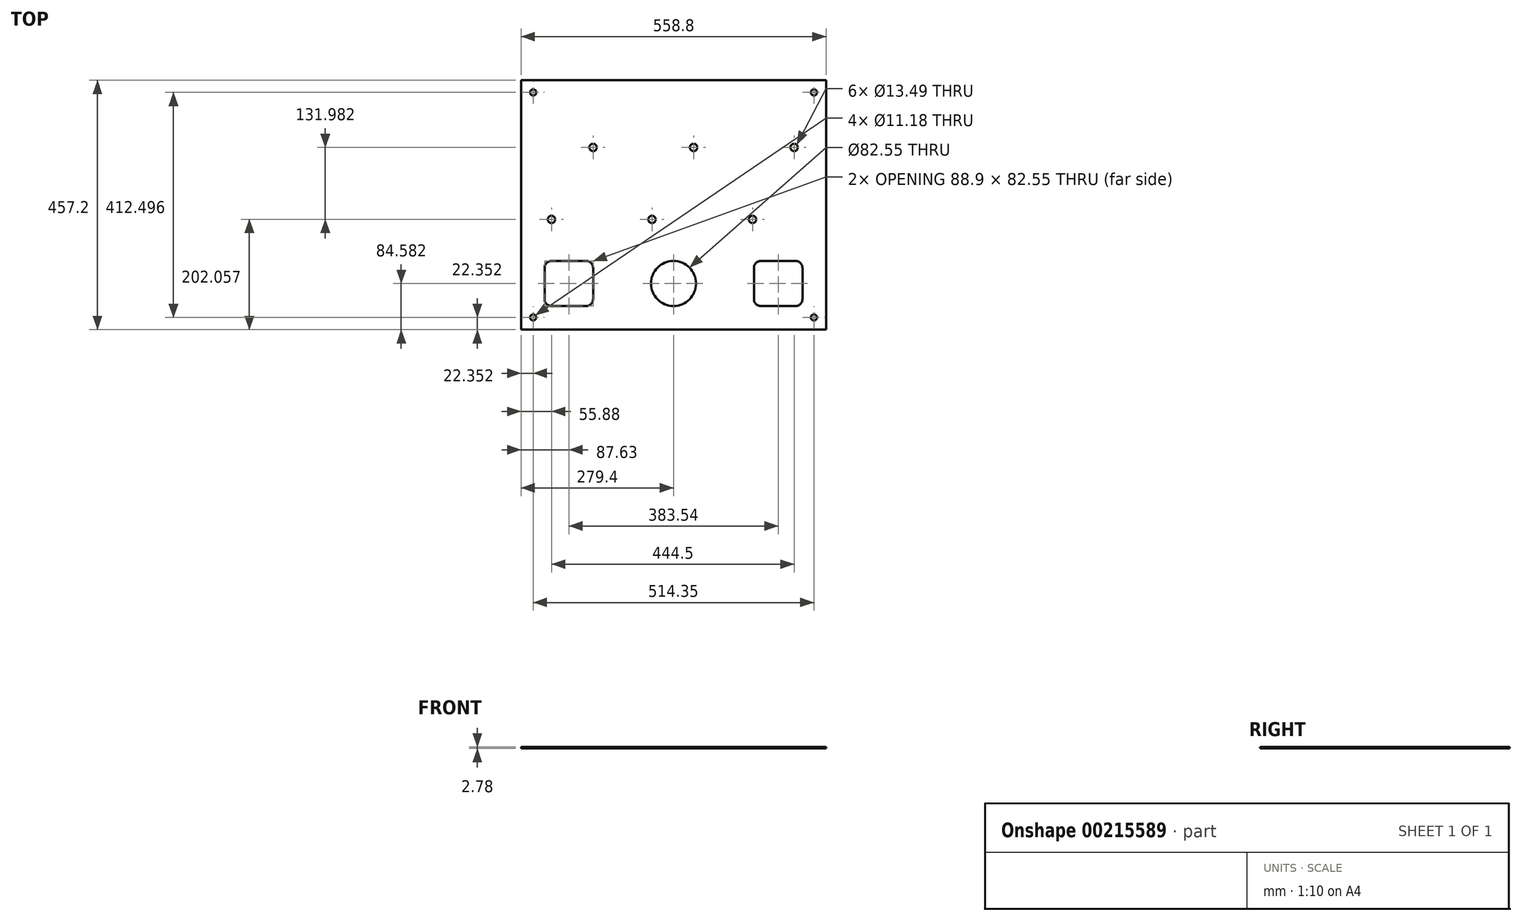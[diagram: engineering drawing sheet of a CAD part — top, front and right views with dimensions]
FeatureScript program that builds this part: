
annotation { "Feature Type Name" : "Feature", "Feature Type Description" : "" }
export const myFeature = defineFeature(function(context is Context, id is Id, definition is map)
    precondition{}
    {
        {
            var Q0;
            Q0=qCreatedBy(makeId("Top.planeOp"),FACE);
            var sketch = newSketch(context, id + "F0", { "sketchPlane" : qUnion([Q0])});
            skLineSegment(sketch, "E0.bottom", {"start": v(0, 0) * mm, "end": v(558.8, 0) * mm});
            skLineSegment(sketch, "E0.top", {"start": v(0, 457.2) * mm, "end": v(558.8, 457.2) * mm});
            skLineSegment(sketch, "E0.left", {"start": v(0, 0) * mm, "end": v(0, 457.2) * mm});
            skLineSegment(sketch, "E0.right", {"start": v(558.8, 0) * mm, "end": v(558.8, 457.2) * mm});
            skCircle(sketch, "E1", {"center": v(22.35, 434.85) * mm, "radius": 5.59 * mm});
            skCircle(sketch, "E2", {"center": v(22.35, 22.35) * mm, "radius": 5.59 * mm});
            skCircle(sketch, "E3", {"center": v(536.7, 22.35) * mm, "radius": 5.59 * mm});
            skCircle(sketch, "E4", {"center": v(536.7, 434.85) * mm, "radius": 5.59 * mm});
            skLineSegment(sketch, "E5.bottom", {"start": v(55.88, 125.86) * mm, "end": v(119.38, 125.86) * mm});
            skLineSegment(sketch, "E5.top", {"start": v(55.88, 43.3) * mm, "end": v(119.38, 43.3) * mm});
            skLineSegment(sketch, "E5.left", {"start": v(43.18, 113.16) * mm, "end": v(43.18, 56) * mm});
            skLineSegment(sketch, "E5.right", {"start": v(132.08, 113.16) * mm, "end": v(132.08, 56) * mm});
            skPoint(sketch, "E6.visualSharp", {"position": v(43.18, 125.86) * mm});
            skArc(sketch, "E6.filletArc", {"start": v(55.88, 125.86) * mm, "mid": v(46.9, 122.14) * mm, "end": v(43.18, 113.16) * mm});
            skPoint(sketch, "E7.visualSharp", {"position": v(132.08, 125.86) * mm});
            skArc(sketch, "E7.filletArc", {"start": v(132.08, 113.16) * mm, "mid": v(128.36, 122.14) * mm, "end": v(119.38, 125.86) * mm});
            skPoint(sketch, "E8.visualSharp", {"position": v(132.08, 43.3) * mm});
            skArc(sketch, "E8.filletArc", {"start": v(119.38, 43.3) * mm, "mid": v(128.36, 47.03) * mm, "end": v(132.08, 56) * mm});
            skPoint(sketch, "E9.visualSharp", {"position": v(43.18, 43.3) * mm});
            skArc(sketch, "E9.filletArc", {"start": v(43.18, 56) * mm, "mid": v(46.9, 47.03) * mm, "end": v(55.88, 43.3) * mm});
            skPoint(sketch, "E10", {"position": v(43.18, 84.58) * mm});
            skPoint(sketch, "E11", {"position": v(279.4, 0) * mm});
            skLineSegment(sketch, "E12", {"start": v(279.4, -97.52) * mm, "end": v(279.4, 529.86) * mm, "construction": true});
            skArc(sketch, "E13.MirrorCS", {"start": v(502.92, 125.86) * mm, "mid": v(511.9, 122.14) * mm, "end": v(515.62, 113.16) * mm});
            skArc(sketch, "E14.MirrorCS", {"start": v(515.62, 56) * mm, "mid": v(511.9, 47.03) * mm, "end": v(502.92, 43.3) * mm});
            skArc(sketch, "E15.MirrorCS", {"start": v(439.42, 43.3) * mm, "mid": v(430.44, 47.03) * mm, "end": v(426.72, 56) * mm});
            skArc(sketch, "E16.MirrorCS", {"start": v(426.72, 113.16) * mm, "mid": v(430.44, 122.14) * mm, "end": v(439.42, 125.86) * mm});
            skLineSegment(sketch, "E17.MirrorCS", {"start": v(426.72, 113.16) * mm, "end": v(426.72, 56) * mm});
            skPoint(sketch, "E18.MirrorP", {"position": v(515.62, 43.3) * mm});
            skLineSegment(sketch, "E19.MirrorCS", {"start": v(515.62, 113.16) * mm, "end": v(515.62, 56) * mm});
            skLineSegment(sketch, "E20.MirrorCS", {"start": v(502.92, 43.3) * mm, "end": v(439.42, 43.3) * mm});
            skPoint(sketch, "E21.MirrorP", {"position": v(515.62, 84.58) * mm});
            skPoint(sketch, "E22.MirrorP", {"position": v(515.62, 125.86) * mm});
            skLineSegment(sketch, "E23.MirrorCS", {"start": v(502.92, 125.86) * mm, "end": v(439.42, 125.86) * mm});
            skPoint(sketch, "E24.MirrorP", {"position": v(426.72, 125.86) * mm});
            skPoint(sketch, "E25.MirrorP", {"position": v(426.72, 43.3) * mm});
            skCircle(sketch, "E26", {"center": v(279.4, 84.58) * mm, "radius": 41.28 * mm});
            skPoint(sketch, "E26.centerSnap0", {"position": v(132.08, 84.58) * mm});
            skCircle(sketch, "E27", {"center": v(55.88, 202.06) * mm, "radius": 6.75 * mm});
            skCircle(sketch, "E28", {"center": v(132.08, 334.04) * mm, "radius": 6.75 * mm});
            skLineSegment(sketch, "E29", {"start": v(55.88, 202.06) * mm, "end": v(132.08, 334.04) * mm, "construction": true});
            skLineSegment(sketch, "E30", {"start": v(55.88, 202.06) * mm, "end": v(55.88, 376.28) * mm, "construction": true});
            skPoint(sketch, "E31", {"position": v(87.63, 125.86) * mm});
            skCircle(sketch, "E32", {"center": v(240.03, 202.06) * mm, "radius": 6.75 * mm});
            skCircle(sketch, "E33", {"center": v(316.23, 334.04) * mm, "radius": 6.75 * mm});
            skLineSegment(sketch, "E34", {"start": v(240.03, 202.06) * mm, "end": v(316.23, 334.04) * mm, "construction": true});
            skLineSegment(sketch, "E35", {"start": v(240.03, 202.06) * mm, "end": v(240.03, 352.53) * mm, "construction": true});
            skCircle(sketch, "E36", {"center": v(424.18, 202.06) * mm, "radius": 6.75 * mm});
            skCircle(sketch, "E37", {"center": v(500.38, 334.04) * mm, "radius": 6.75 * mm});
            skLineSegment(sketch, "E38", {"start": v(424.18, 202.06) * mm, "end": v(500.38, 334.04) * mm, "construction": true});
            skLineSegment(sketch, "E39", {"start": v(424.18, 202.06) * mm, "end": v(424.18, 281.3) * mm, "construction": true});
            skSolve(sketch);
        }
        {
            var Q0;
            Q0=makeQuery(id+"F0.imprint","IMPRINT",FACE,{"disambiguationData":[TD([[makeQuery(id+"F0.imprint","IMPRINT",EDGE,{"derivedFrom":sQuery(id+"F0.wireOp",EDGE,"E0.bottom")}),1.0]])]});
            extrude(context, id + "F1", {"entities" : qUnion([Q0]), "depth" : 2.78 * mm});
        }
    });
